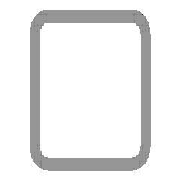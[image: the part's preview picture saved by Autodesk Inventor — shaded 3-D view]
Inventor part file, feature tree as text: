
AUTODESK INVENTOR PART (.ipt)
format: ipt  version: 2025 (Build 290162010, 162A)  size: 134,656 bytes
history: native  units: mm (DEFAULTED — no unit token found)
features: other x4, sketch x1, plane x1
ambient origin geometry x8: Origin, YZ Plane, XZ Plane, XY Plane, X Axis, Y Axis, Z Axis, Center Point
bodies: Solid1 (feature_tree), Body (feature_tree)
feature tree (6):
  parser-record x1  (decoder bookkeeping rows leaked as tree rows — omitted from the tree; the rows remain in map.json)
  other  "Driven Length"
  other  "Start Plane"
  other  "End Plane"
  sketch  "Sketch3"  dims[d3=1264.624682mm d4=0.0mm d7=6.0mm d9=80.0mm d11=80.0mm d12=3.0mm d13=40.0mm d14=1304.624682mm d15=40.0mm d16=40.0mm d17=90.0deg d18=1264.624682mm]
  plane  "Work Plane3"
